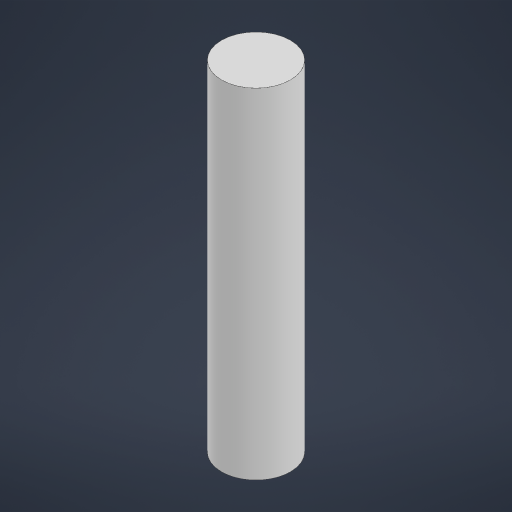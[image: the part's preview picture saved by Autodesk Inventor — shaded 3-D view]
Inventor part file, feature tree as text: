
AUTODESK INVENTOR PART (.ipt)
format: ipt  version: 2023 (Build 270158030, 158C)  size: 155,648 bytes
history: native  units: in
note: dims shown in document units (in); Inventor stores cm internally (conversion verified against a paired STEP export)
features: extrude x1, sketch x1
ambient origin geometry x8: Origin, YZ Plane, XZ Plane, XY Plane, X Axis, Y Axis, Z Axis, Center Point
bodies: Solid1 (feature_tree)
feature tree (2):
  extrude  "Extrusion1"  Depth=1.4961in TaperAngle=0.0deg
  sketch  "Sketch2"  dims[d0=0.3031in d1=1.4961in d2=0.0in]
